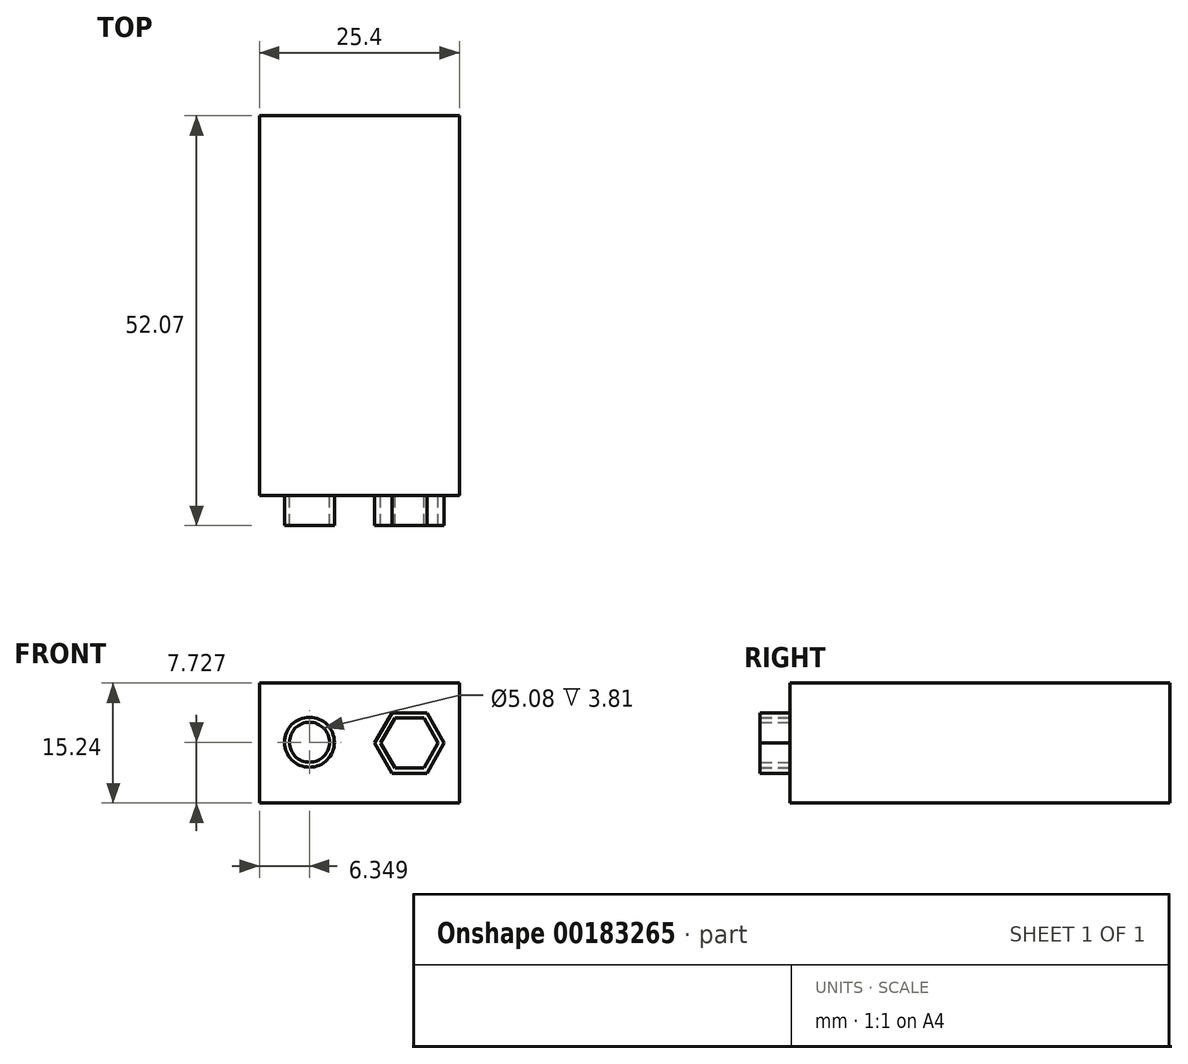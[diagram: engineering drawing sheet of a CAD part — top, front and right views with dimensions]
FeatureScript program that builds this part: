
annotation { "Feature Type Name" : "Feature", "Feature Type Description" : "" }
export const myFeature = defineFeature(function(context is Context, id is Id, definition is map)
    precondition{}
    {
        {
            var Q0;
            Q0=qCreatedBy(makeId("Top.planeOp"),FACE);
            var sketch = newSketch(context, id + "F0", { "sketchPlane" : qUnion([Q0])});
            skLineSegment(sketch, "E0.bottom", {"start": v(0, 0) * mm, "end": v(25.4, 0) * mm});
            skLineSegment(sketch, "E0.top", {"start": v(0, 48.26) * mm, "end": v(25.4, 48.26) * mm});
            skLineSegment(sketch, "E0.left", {"start": v(0, 0) * mm, "end": v(0, 48.26) * mm});
            skLineSegment(sketch, "E0.right", {"start": v(25.4, 0) * mm, "end": v(25.4, 48.26) * mm});
            skSolve(sketch);
        }
        {
            var Q0;
            Q0=makeQuery(id+"F0.imprint","IMPRINT",FACE,{"disambiguationData":[TD([[makeQuery(id+"F0.imprint","IMPRINT",EDGE,{"derivedFrom":sQuery(id+"F0.wireOp",EDGE,"E0.bottom")}),1.0]])]});
            extrude(context, id + "F1", {"entities" : qUnion([Q0]), "depth" : 15.24 * mm});
        }
        {
            var Q0;
            Q0=makeQuery(id+"F1.opExtrude","SWEPT_FACE",FACE,{"disambiguationData":[OSD([sQuery(id+"F0.wireOp",EDGE,"E0.bottom")])]});
            var sketch = newSketch(context, id + "F2", { "sketchPlane" : qUnion([Q0])});
            skCircle(sketch, "E1", {"center": v(6.35, 7.73) * mm, "radius": 3.18 * mm});
            skCircle(sketch, "E2", {"center": v(6.35, 7.73) * mm, "radius": 2.54 * mm});
            skSolve(sketch);
        }
        {
            var Q0;
            Q0=makeQuery(id+"F2.imprint","IMPRINT",FACE,{"disambiguationData":[TD([[makeQuery(id+"F2.imprint","IMPRINT",EDGE,{"derivedFrom":sQuery(id+"F2.wireOp",EDGE,"E1")}),1.0]])]});
            extrude(context, id + "F3", {"entities" : qUnion([Q0]), "operationType" : NewBodyOperationType.ADD, "depth" : 3.8 * mm});
        }
        {
            var Q0;
            {var subQ1=sQuery(id+"F0.wireOp",EDGE,"E0.left");var subQ3=sQuery(id+"F0.wireOp",EDGE,"E0.bottom");Q0=makeQuery(id+"F3.boolean.opBoolean","SPLIT",FACE,{"disambiguationData":[TD([makeQuery(id+"F1.opExtrude","SWEPT_FACE",FACE,{"disambiguationData":[OSD([subQ1])]})])],"derivedFrom":makeQuery(id+"F1.opExtrude","SWEPT_FACE",FACE,{"disambiguationData":[OSD([subQ3])]})});}
            var sketch = newSketch(context, id + "F4", { "sketchPlane" : qUnion([Q0])});
            skCircle(sketch, "E3.cCircle", {"center": v(19.05, 7.62) * mm, "radius": 3.67 * mm, "construction": true});
            skLineSegment(sketch, "E3.0", {"start": v(20.88, 4.44) * mm, "end": v(17.22, 4.44) * mm});
            skLineSegment(sketch, "E3.1", {"start": v(17.22, 4.44) * mm, "end": v(15.38, 7.62) * mm});
            skLineSegment(sketch, "E3.2", {"start": v(15.38, 7.62) * mm, "end": v(17.22, 10.8) * mm});
            skLineSegment(sketch, "E3.3", {"start": v(17.22, 10.8) * mm, "end": v(20.88, 10.8) * mm});
            skLineSegment(sketch, "E3.4", {"start": v(20.88, 10.8) * mm, "end": v(22.72, 7.62) * mm});
            skLineSegment(sketch, "E3.5", {"start": v(22.72, 7.62) * mm, "end": v(20.88, 4.45) * mm});
            skCircle(sketch, "E4.cCircle", {"center": v(19.05, 7.62) * mm, "radius": 4.42 * mm, "construction": true});
            skLineSegment(sketch, "E4.0", {"start": v(21.26, 11.45) * mm, "end": v(23.47, 7.62) * mm});
            skLineSegment(sketch, "E4.1", {"start": v(23.47, 7.62) * mm, "end": v(21.26, 3.79) * mm});
            skLineSegment(sketch, "E4.2", {"start": v(21.26, 3.79) * mm, "end": v(16.84, 3.79) * mm});
            skLineSegment(sketch, "E4.3", {"start": v(16.84, 3.79) * mm, "end": v(14.63, 7.62) * mm});
            skLineSegment(sketch, "E4.4", {"start": v(14.63, 7.62) * mm, "end": v(16.84, 11.45) * mm});
            skLineSegment(sketch, "E4.5", {"start": v(16.84, 11.45) * mm, "end": v(21.26, 11.45) * mm});
            skSolve(sketch);
        }
        {
            var Q0;
            Q0=makeQuery(id+"F4.imprint","IMPRINT",FACE,{"disambiguationData":[TD([[makeQuery(id+"F4.imprint","IMPRINT",EDGE,{"derivedFrom":sQuery(id+"F4.wireOp",EDGE,"E3.0")}),1.0]])]});
            extrude(context, id + "F5", {"entities" : qUnion([Q0]), "operationType" : NewBodyOperationType.ADD, "depth" : 3.8 * mm});
        }
    });
